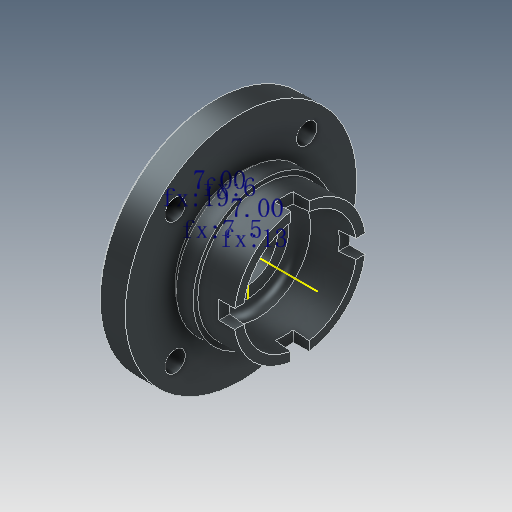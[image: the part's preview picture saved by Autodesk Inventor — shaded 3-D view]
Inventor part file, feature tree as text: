
AUTODESK INVENTOR PART (.ipt)
format: ipt  version: 2025 (Build 290162000, 162)  size: 252,416 bytes
history: native  units: in
note: dims shown in document units (in); Inventor stores cm internally (conversion verified against a paired STEP export)
features: sketch x6, extrude x3, revolve x2, chamfer x1, fillet x1
ambient origin geometry x8: Origin, YZ Plane, XZ Plane, XY Plane, X Axis, Y Axis, Z Axis, Center Point
bodies: 实体1 (feature_tree)
feature tree (13):
  revolve  "旋转1"  [1 undecoded]
  extrude  "拉伸1"  Depth=0.4724in
  extrude  "拉伸2"  Depth=1.1417in
  extrude  "拉伸3"  Depth=0.3937in
  chamfer  "倒角1"  Distance=0.0394in
  fillet  "圆角1"  Radius=0.5906in
  sketch  "草图5"  dims[d11=45.0deg d12=0.0394in d13=0.5906in d14=0.9843in d15=0.5792in d16=90.0deg d17=0.2756in d18=0.315in d19=0.0in d20=0.2756in d21=0.315in d22=0.0in d23=0.3543in d24=1.6142in d25=1.5748in d27=360.0deg d29=0.315in d30=0.0in d31=0.0394in d32=0.0787in d33=45.0deg d34=0.1969in d35=0.5118in d36=0.748in d37=0.2362in d38=0.0481in d39=0.0481in d40=0.2953in d41=90.0deg d42=45.0deg]
  revolve  "旋转2"  [1 undecoded]
  sketch  "草图1"  dims[d3=0.315in d0=0.3543in d1=1.0236in d2=2.0079in]
  sketch  "草图2"  dims[d6=1.2205in d7=1.1417in]
  sketch  "草图3"  dims[d8=0.3937in d9=0.0984in]
  sketch  "草图4"  dims[d10=1.1417in]
  sketch  "草图 - 环形阵列1"  dims[d4=1.0236in d5=0.4724in]
note: 2 required parameter values undecoded (feature->parameter linkage not recoverable at this tier; creation-order binding heuristic only, values carry confidence <= 0.55)
